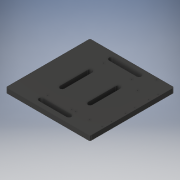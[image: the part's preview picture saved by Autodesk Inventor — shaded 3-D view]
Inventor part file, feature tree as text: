
AUTODESK INVENTOR PART (.ipt)
format: ipt  version: 2017 (Build 210142000, 142)  size: 219,136 bytes
history: native  units: in
note: dims shown in document units (in); Inventor stores cm internally (conversion verified against a paired STEP export)
features: extrude x6, sketch x6, projected_geometry x2, fillet x1
ambient origin geometry x8: Origin, YZ Plane, XZ Plane, XY Plane, X Axis, Y Axis, Z Axis, Center Point
bodies: Solid1 (feature_tree)
feature tree (15):
  extrude  "Extrusion1"  Depth=9.0in
  fillet  "Fillet1"  Radius=3.0in
  extrude  "camMount"  Depth=0.125in
  extrude  "TilitMount"  Depth=0.125in
  extrude  "Extrusion6"  Depth=3.0in
  extrude  "Extrusion7"  Depth=0.125in
  extrude  "Extrusion8"  Depth=0.125in
  sketch  "Sketch1"  dims[d0=9.0in d1=9.0in d2=3.0in]
  sketch  "Sketch4"  dims[d3=1.5in d4=0.125in]
  projected_geometry  "Projected Loop2"
  sketch  "Sketch5"  dims[d5=3.0in d6=0.125in]
  projected_geometry  "Projected Loop3"
  sketch  "Sketch6"  dims[d7=1.5in d8=3.0in]
  sketch  "Sketch7"  dims[d9=0.125in d10=0.125in]
  sketch  "Sketch8"  dims[d11=0.5in d12=0.0in d21=0.125in d22=1.625in d23=0.25in d24=2.25in d25=0.125in d26=0.125in d27=1.0in d28=0.0in d29=0.25in d30=1.465in d31=2.152in d34=1.0in d35=0.0in d36=3.402in d37=1.5in d38=0.125in d39=3.0in d40=7.5in d41=0.5in d42=0.5in d43=3.0in d44=0.5in d45=0.5in d46=1.0in d47=0.0in d48=0.375in d49=0.5in d50=0.125in d51=1.0in d52=0.0in d53=1.5in d54=1.0in d55=0.125in d56=0.125in d57=1.0in d58=0.0in]
